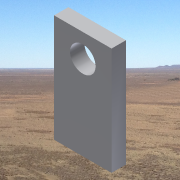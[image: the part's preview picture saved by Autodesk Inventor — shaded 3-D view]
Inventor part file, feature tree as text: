
AUTODESK INVENTOR PART (.ipt)
format: ipt  version: 2014 SP1 (Build 180222100, 222)  size: 137,728 bytes
history: native  units: in
note: dims shown in document units (in); Inventor stores cm internally (conversion verified against a paired STEP export)
features: sketch x3, extrude x2, hole x1
ambient origin geometry x8: Origin, YZ Plane, XZ Plane, XY Plane, X Axis, Y Axis, Z Axis, Center Point
bodies: Solid1 (feature_tree)
feature tree (6):
  extrude  "Extrusion1"  Depth=3.75in
  extrude  "Extrusion2"  Depth=0.5in
  hole  "Hole1"  [1 undecoded]
  sketch  "Sketch1"  dims[d0=2.0in d1=3.75in]
  sketch  "Sketch2"  dims[d2=0.5in d3=0.0in d4=2.935in]
  sketch  "Sketch3"  dims[d5=0.89in d6=0.5in d7=0.0in d8=0.719in d9=0.13in d10=0.5in d11=0.375in d12=0.25in d13=0.5635in d14=0.6in d15=0.8108in]
note: 1 required parameter value undecoded (feature->parameter linkage not recoverable at this tier; creation-order binding heuristic only, values carry confidence <= 0.55)
